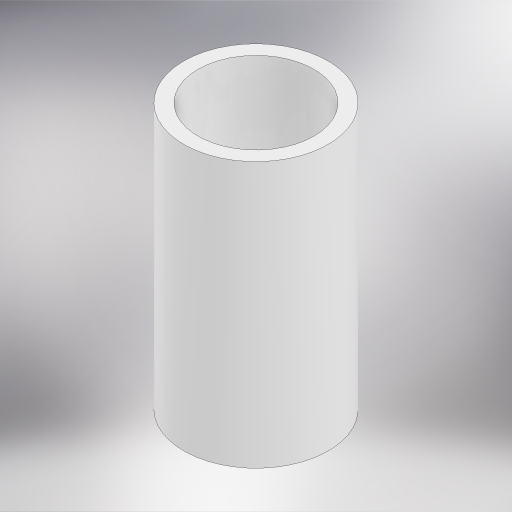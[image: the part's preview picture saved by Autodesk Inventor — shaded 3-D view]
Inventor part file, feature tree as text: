
AUTODESK INVENTOR PART (.ipt)
format: ipt  version: 2023 (Build 270158000, 158)  size: 271,360 bytes
history: native  units: in
note: dims shown in document units (in); Inventor stores cm internally (conversion verified against a paired STEP export)
features: other x1, extrude x1, sketch x1
ambient origin geometry x8: Origin, YZ Plane, XZ Plane, XY Plane, X Axis, Y Axis, Z Axis, Center Point
bodies: Body1 (feature_tree)
feature tree (3):
  other  "Sólido1"
  extrude  "Extrusión1"  Depth=1.9291in
  sketch  "Boceto2"  dims[d1=1.0492in d2=0.8425in d3=1.9291in d4=0.0in]
